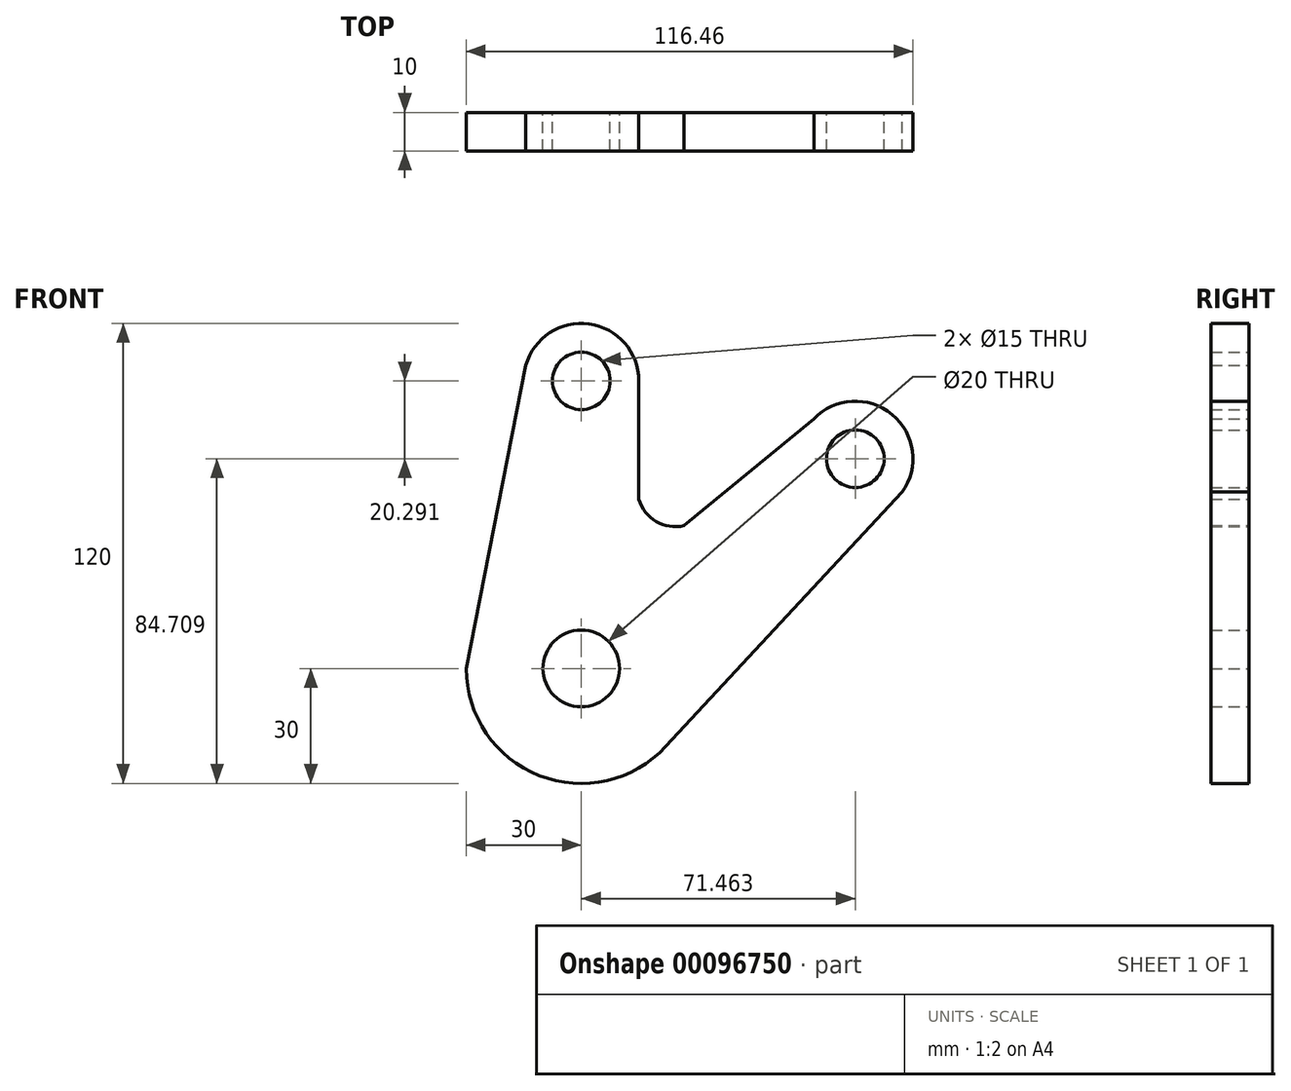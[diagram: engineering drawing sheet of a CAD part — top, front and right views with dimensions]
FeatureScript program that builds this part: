
annotation { "Feature Type Name" : "Feature", "Feature Type Description" : "" }
export const myFeature = defineFeature(function(context is Context, id is Id, definition is map)
    precondition{}
    {
        {
            var Q0;
            Q0=qCreatedBy(makeId("Front.planeOp"),FACE);
            var sketch = newSketch(context, id + "F0", { "sketchPlane" : qUnion([Q0])});
            skCircle(sketch, "E0", {"center": v(0, 0) * mm, "radius": 10 * mm});
            skArc(sketch, "E1", {"start": v(-30, 0) * mm, "mid": v(-10.94, -27.93) * mm, "end": v(22.02, -20.38) * mm});
            skLineSegment(sketch, "E2", {"start": v(-30, 0) * mm, "end": v(-14.44, 79.05) * mm});
            skLineSegment(sketch, "E3", {"start": v(22.02, -20.38) * mm, "end": v(83.68, 46.01) * mm});
            skCircle(sketch, "E4", {"center": v(0, 75) * mm, "radius": 7.5 * mm});
            skArc(sketch, "E5", {"start": v(-14.44, 79.05) * mm, "mid": v(2.04, 89.86) * mm, "end": v(15, 75) * mm});
            skCircle(sketch, "E6", {"center": v(71.46, 54.7) * mm, "radius": 7.5 * mm});
            skArc(sketch, "E7", {"start": v(83.68, 46.01) * mm, "mid": v(81.03, 66.26) * mm, "end": v(60.63, 65.09) * mm});
            skLineSegment(sketch, "E8", {"start": v(15, 75) * mm, "end": v(15, 44.11) * mm});
            skLineSegment(sketch, "E9", {"start": v(60.63, 65.09) * mm, "end": v(26.8, 37.26) * mm});
            skArc(sketch, "E10", {"start": v(15, 44.11) * mm, "mid": v(19.55, 38.36) * mm, "end": v(26.8, 37.26) * mm});
            skSolve(sketch);
        }
        {
            var Q0;
            Q0 = qSketchRegion(id + "F0", true);
            extrude(context, id + "F1", {"entities" : qUnion([Q0]), "depth" : 10 * mm});
        }
    });
